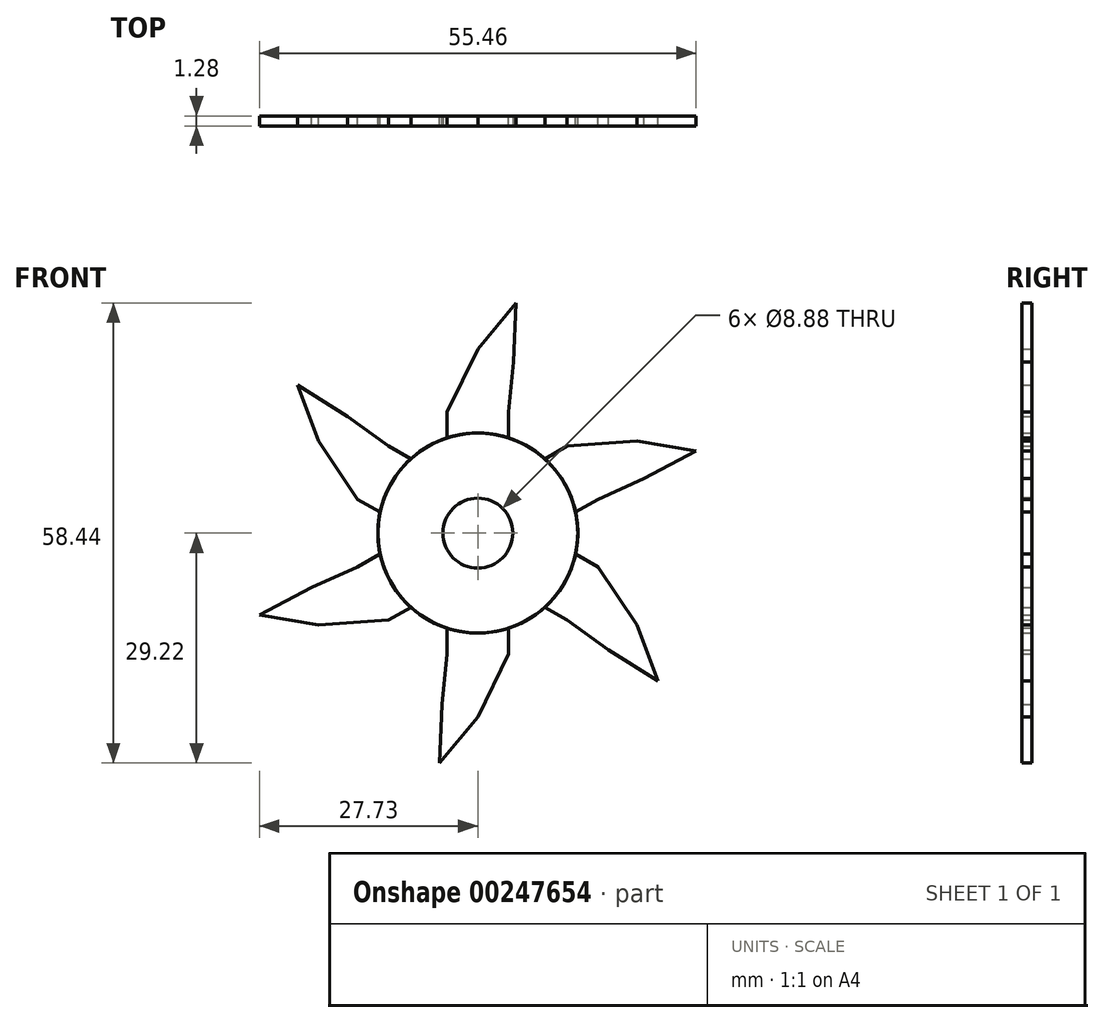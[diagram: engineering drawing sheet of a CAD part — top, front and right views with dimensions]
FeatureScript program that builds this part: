
annotation { "Feature Type Name" : "Feature", "Feature Type Description" : "" }
export const myFeature = defineFeature(function(context is Context, id is Id, definition is map)
    precondition{}
    {
        {
            var Q0;
            Q0=qCreatedBy(makeId("Front.planeOp"),FACE);
            var sketch = newSketch(context, id + "F0", { "sketchPlane" : qUnion([Q0])});
            skCircle(sketch, "E0", {"center": v(0, 0) * mm, "radius": 12.7 * mm});
            skSolve(sketch);
        }
        {
            var Q0;
            Q0=qSketchRegion(id+"F0",true);
            extrude(context, id + "F1", {"entities" : qUnion([Q0]), "depth" : 1.27 * mm, "symmetric" : true});
        }
        {
            var Q0;
            Q0=qCreatedBy(makeId("Front.planeOp"),FACE);
            var sketch = newSketch(context, id + "F2", { "sketchPlane" : qUnion([Q0])});
            skLineSegment(sketch, "E1.bottom", {"start": v(3.9, 15.36) * mm, "end": v(-3.9, 15.36) * mm});
            skLineSegment(sketch, "E1.top", {"start": v(3.9, 9.4) * mm, "end": v(-3.9, 9.4) * mm});
            skLineSegment(sketch, "E1.left", {"start": v(3.9, 15.36) * mm, "end": v(3.9, 9.4) * mm});
            skLineSegment(sketch, "E1.right", {"start": v(-3.9, 15.36) * mm, "end": v(-3.9, 9.4) * mm});
            skPoint(sketch, "E1.middle", {"position": v(0, 12.38) * mm});
            skLineSegment(sketch, "E2", {"start": v(-3.9, 15.36) * mm, "end": v(0, 23.36) * mm});
            skLineSegment(sketch, "E3", {"start": v(0, 23.36) * mm, "end": v(4.55, 21.76) * mm});
            skLineSegment(sketch, "E4", {"start": v(4.55, 21.76) * mm, "end": v(3.9, 15.36) * mm});
            skLineSegment(sketch, "E5", {"start": v(0, 23.36) * mm, "end": v(4.86, 29.22) * mm});
            skLineSegment(sketch, "E6", {"start": v(4.86, 29.22) * mm, "end": v(4.55, 21.76) * mm});
            skSolve(sketch);
        }
        {
            var Q0;
            Q0=qSketchRegion(id+"F2",true);
            extrude(context, id + "F3", {"entities" : qUnion([Q0]), "operationType" : NewBodyOperationType.ADD, "depth" : 1.27 * mm, "symmetric" : true});
        }
        {
            var Q0;
            Q0=makeQuery(id+"F1.opExtrude","SWEPT_BODY",BODY,{"disambiguationData":[OSD([sQuery(id+"F0.wireOp",EDGE,"E0")])]});
            var Q1;
            Q1=sQuery(id+"F0.wireOp",EDGE,"E0");
            circularPattern(context, id + "F4", {"entities" : qUnion([Q0]), "axis" : qUnion([Q1]), "angle" : 360 * degree, "instanceCount" : 6, "equalSpace" : true});
        }
        {
            var Q0;
            Q0=qCreatedBy(makeId("Front.planeOp"),FACE);
            var sketch = newSketch(context, id + "F5", { "sketchPlane" : qUnion([Q0])});
            skCircle(sketch, "E7", {"center": v(0, 0) * mm, "radius": 4.44 * mm});
            skSolve(sketch);
        }
        {
            var Q0;
            Q0=qSketchRegion(id+"F5",true);
            extrude(context, id + "F6", {"entities" : qUnion([Q0]), "operationType" : NewBodyOperationType.REMOVE, "oppositeDirection" : true, "depth" : 1.27 * mm, "symmetric" : true});
        }
    });
